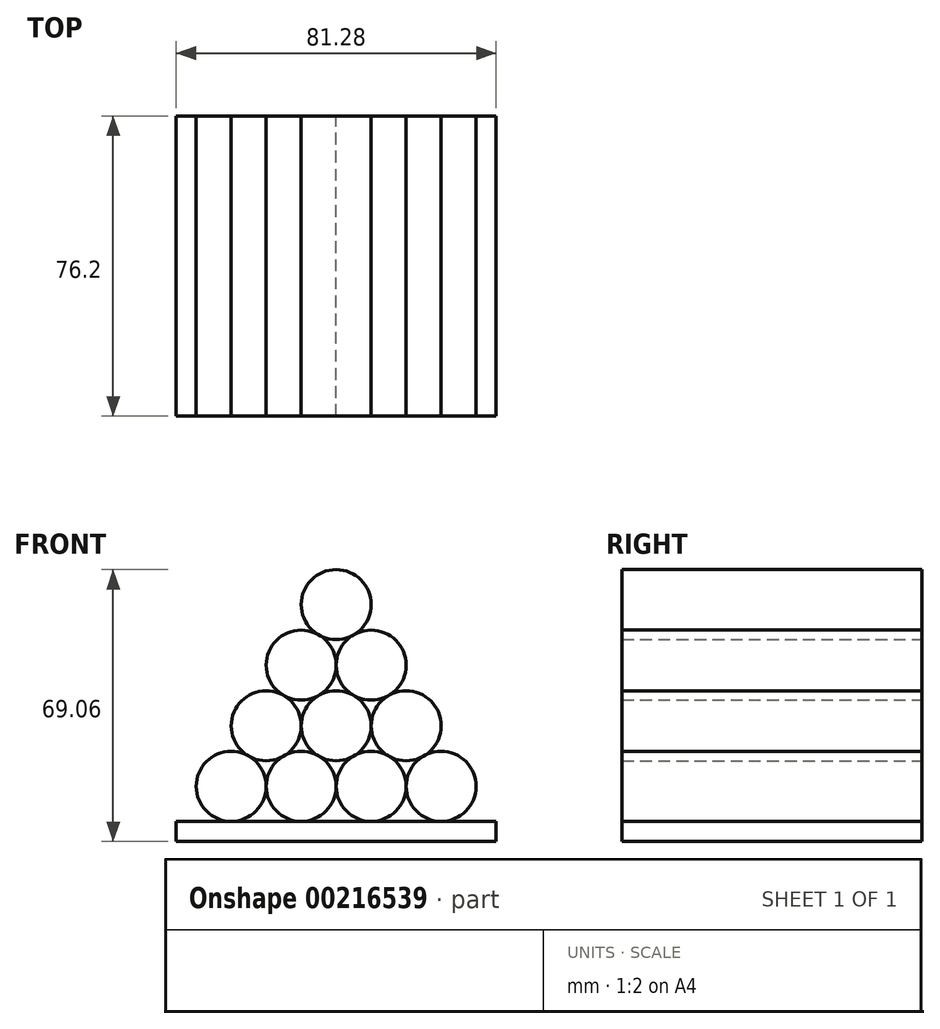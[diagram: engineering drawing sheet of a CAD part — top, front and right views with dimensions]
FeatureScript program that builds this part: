
annotation { "Feature Type Name" : "Feature", "Feature Type Description" : "" }
export const myFeature = defineFeature(function(context is Context, id is Id, definition is map)
    precondition{}
    {
        {
            var Q0;
            Q0=qCreatedBy(makeId("Front.planeOp"),FACE);
            var sketch = newSketch(context, id + "F0", { "sketchPlane" : qUnion([Q0])});
            skCircle(sketch, "E0", {"center": v(-26.67, 0) * mm, "radius": 8.9 * mm});
            skCircle(sketch, "E1", {"center": v(-8.9, 0) * mm, "radius": 8.9 * mm});
            skCircle(sketch, "E2", {"center": v(8.9, 0) * mm, "radius": 8.9 * mm});
            skCircle(sketch, "E3", {"center": v(-17.78, 15.4) * mm, "radius": 8.9 * mm});
            skCircle(sketch, "E4", {"center": v(0, 15.4) * mm, "radius": 8.9 * mm});
            skCircle(sketch, "E5", {"center": v(-8.9, 30.8) * mm, "radius": 8.9 * mm});
            skCircle(sketch, "E6", {"center": v(-35.56, -15.4) * mm, "radius": 8.9 * mm});
            skCircle(sketch, "E7", {"center": v(-17.78, -15.4) * mm, "radius": 8.9 * mm});
            skCircle(sketch, "E8", {"center": v(0, -15.4) * mm, "radius": 8.9 * mm});
            skCircle(sketch, "E9", {"center": v(17.78, -15.4) * mm, "radius": 8.9 * mm});
            skLineSegment(sketch, "E10.bottom", {"start": v(-49.53, -24.29) * mm, "end": v(31.75, -24.29) * mm});
            skLineSegment(sketch, "E10.top", {"start": v(-49.53, -29.37) * mm, "end": v(31.75, -29.37) * mm});
            skLineSegment(sketch, "E10.left", {"start": v(-49.53, -24.29) * mm, "end": v(-49.53, -29.37) * mm});
            skLineSegment(sketch, "E10.right", {"start": v(31.75, -24.29) * mm, "end": v(31.75, -29.37) * mm});
            skLineSegment(sketch, "E11", {"start": v(-8.9, 30.8) * mm, "end": v(-8.9, -46.28) * mm, "construction": true});
            skSolve(sketch);
        }
        {
            var Q0;
            {var subQ0=sQuery(id+"F0.wireOp",EDGE,"E3");var subQ1=makeQuery(id+"F0.imprint","INTERSECT",VERTEX,{"derivedFrom":[sQuery(id+"F0.wireOp",EDGE,"E0"),subQ0]});Q0=makeQuery(id+"F0.imprint","IMPRINT",FACE,{"disambiguationData":[TD([[makeQuery(id+"F0.imprint","IMPRINT",EDGE,{"disambiguationData":[TD([[subQ1,1.0]])],"derivedFrom":subQ0}),1.0]])]});}
            var Q1;
            {var subQ0=sQuery(id+"F0.wireOp",EDGE,"E4");var subQ1=makeQuery(id+"F0.imprint","INTERSECT",VERTEX,{"derivedFrom":[sQuery(id+"F0.wireOp",EDGE,"E3"),subQ0]});Q1=makeQuery(id+"F0.imprint","IMPRINT",FACE,{"disambiguationData":[TD([[makeQuery(id+"F0.imprint","IMPRINT",EDGE,{"disambiguationData":[TD([[subQ1,1.0]])],"derivedFrom":subQ0}),1.0]])]});}
            var Q2;
            {var subQ0=sQuery(id+"F0.wireOp",EDGE,"E5");var subQ1=makeQuery(id+"F0.imprint","INTERSECT",VERTEX,{"derivedFrom":[sQuery(id+"F0.wireOp",EDGE,"E4"),subQ0]});Q2=makeQuery(id+"F0.imprint","IMPRINT",FACE,{"disambiguationData":[TD([[makeQuery(id+"F0.imprint","IMPRINT",EDGE,{"disambiguationData":[TD([[subQ1,-1.0]])],"derivedFrom":subQ0}),1.0]])]});}
            var Q3;
            {var subQ0=sQuery(id+"F0.wireOp",EDGE,"6513f72b-f417-4675-a262-e46438cbcac2");var subQ1=makeQuery(id+"F0.imprint","INTERSECT",VERTEX,{"derivedFrom":[subQ0,sQuery(id+"F0.wireOp",EDGE,"E5")]});Q3=makeQuery(id+"F0.imprint","IMPRINT",FACE,{"disambiguationData":[TD([[makeQuery(id+"F0.imprint","IMPRINT",EDGE,{"disambiguationData":[TD([[subQ1,-1.0]])],"derivedFrom":subQ0}),1.0]])]});}
            var Q4;
            {var subQ0=sQuery(id+"F0.wireOp",EDGE,"E2");var subQ4=makeQuery(id+"F0.imprint","INTERSECT",VERTEX,{"derivedFrom":[subQ0,sQuery(id+"F0.wireOp",EDGE,"E5")]});Q4=makeQuery(id+"F0.imprint","IMPRINT",FACE,{"disambiguationData":[TD([[makeQuery(id+"F0.imprint","IMPRINT",EDGE,{"disambiguationData":[TD([[subQ4,1.0]])],"derivedFrom":subQ0}),1.0]])]});}
            var Q5;
            {var subQ0=sQuery(id+"F0.wireOp",EDGE,"E1");var subQ4=makeQuery(id+"F0.imprint","INTERSECT",VERTEX,{"derivedFrom":[subQ0,sQuery(id+"F0.wireOp",EDGE,"E4")]});Q5=makeQuery(id+"F0.imprint","IMPRINT",FACE,{"disambiguationData":[TD([[makeQuery(id+"F0.imprint","IMPRINT",EDGE,{"disambiguationData":[TD([[subQ4,1.0]])],"derivedFrom":subQ0}),1.0]])]});}
            var Q6;
            {var subQ0=sQuery(id+"F0.wireOp",EDGE,"E0");var subQ1=makeQuery(id+"F0.imprint","INTERSECT",VERTEX,{"derivedFrom":[subQ0,sQuery(id+"F0.wireOp",EDGE,"E3")]});Q6=makeQuery(id+"F0.imprint","IMPRINT",FACE,{"disambiguationData":[TD([[makeQuery(id+"F0.imprint","IMPRINT",EDGE,{"disambiguationData":[TD([[subQ1,1.0]])],"derivedFrom":subQ0}),1.0]])]});}
            var Q7;
            {var subQ0=sQuery(id+"F0.wireOp",EDGE,"E6");var subQ1=makeQuery(id+"F0.imprint","INTERSECT",VERTEX,{"derivedFrom":[sQuery(id+"F0.wireOp",EDGE,"E0"),subQ0]});Q7=makeQuery(id+"F0.imprint","IMPRINT",FACE,{"disambiguationData":[TD([[makeQuery(id+"F0.imprint","IMPRINT",EDGE,{"disambiguationData":[TD([[subQ1,1.0]])],"derivedFrom":subQ0}),1.0]])]});}
            var Q8;
            {var subQ0=sQuery(id+"F0.wireOp",EDGE,"E7");var subQ4=makeQuery(id+"F0.imprint","INTERSECT",VERTEX,{"derivedFrom":[sQuery(id+"F0.wireOp",EDGE,"E1"),subQ0]});Q8=makeQuery(id+"F0.imprint","IMPRINT",FACE,{"disambiguationData":[TD([[makeQuery(id+"F0.imprint","IMPRINT",EDGE,{"disambiguationData":[TD([[subQ4,1.0]])],"derivedFrom":subQ0}),1.0]])]});}
            var Q9;
            {var subQ0=sQuery(id+"F0.wireOp",EDGE,"E8");var subQ4=makeQuery(id+"F0.imprint","INTERSECT",VERTEX,{"derivedFrom":[sQuery(id+"F0.wireOp",EDGE,"E2"),subQ0]});Q9=makeQuery(id+"F0.imprint","IMPRINT",FACE,{"disambiguationData":[TD([[makeQuery(id+"F0.imprint","IMPRINT",EDGE,{"disambiguationData":[TD([[subQ4,1.0]])],"derivedFrom":subQ0}),1.0]])]});}
            var Q10;
            {var subQ0=sQuery(id+"F0.wireOp",EDGE,"E9");var subQ4=makeQuery(id+"F0.imprint","INTERSECT",VERTEX,{"derivedFrom":[sQuery(id+"F0.wireOp",EDGE,"6513f72b-f417-4675-a262-e46438cbcac2"),subQ0]});Q10=makeQuery(id+"F0.imprint","IMPRINT",FACE,{"disambiguationData":[TD([[makeQuery(id+"F0.imprint","IMPRINT",EDGE,{"disambiguationData":[TD([[subQ4,1.0]])],"derivedFrom":subQ0}),1.0]])]});}
            var Q11;
            {var subQ0=sQuery(id+"F0.wireOp",EDGE,"c8ee9c56-d4f2-4476-a657-07a7fd572b9a");var subQ1=makeQuery(id+"F0.imprint","INTERSECT",VERTEX,{"derivedFrom":[sQuery(id+"F0.wireOp",EDGE,"6513f72b-f417-4675-a262-e46438cbcac2"),subQ0]});Q11=makeQuery(id+"F0.imprint","IMPRINT",FACE,{"disambiguationData":[TD([[makeQuery(id+"F0.imprint","IMPRINT",EDGE,{"disambiguationData":[TD([[subQ1,-1.0]])],"derivedFrom":subQ0}),1.0]])]});}
            var Q12;
            Q12=makeQuery(id+"F0.imprint","IMPRINT",FACE,{"disambiguationData":[TD([[makeQuery(id+"F0.imprint","IMPRINT",EDGE,{"derivedFrom":sQuery(id+"F0.wireOp",EDGE,"E10.top")}),1.0]])]});
            var Q13;
            Q13=sQuery(id+"F0.wireOp",EDGE,"E4");
            var Q14;
            Q14=sQuery(id+"F0.wireOp",EDGE,"E5");
            var Q15;
            Q15=sQuery(id+"F0.wireOp",EDGE,"E10.bottom");
            var Q16;
            Q16=sQuery(id+"F0.wireOp",EDGE,"E1");
            var Q17;
            Q17=sQuery(id+"F0.wireOp",EDGE,"6513f72b-f417-4675-a262-e46438cbcac2");
            var Q18;
            Q18=sQuery(id+"F0.wireOp",EDGE,"E3");
            var Q19;
            Q19=sQuery(id+"F0.wireOp",EDGE,"c8ee9c56-d4f2-4476-a657-07a7fd572b9a");
            var Q20;
            Q20=sQuery(id+"F0.wireOp",EDGE,"E7");
            var Q21;
            Q21=sQuery(id+"F0.wireOp",EDGE,"E2");
            var Q22;
            Q22=sQuery(id+"F0.wireOp",EDGE,"E10.top");
            var Q23;
            Q23=sQuery(id+"F0.wireOp",EDGE,"E0");
            var Q24;
            Q24=sQuery(id+"F0.wireOp",EDGE,"E8");
            var Q25;
            Q25=sQuery(id+"F0.wireOp",EDGE,"E9");
            var Q26;
            Q26=sQuery(id+"F0.wireOp",EDGE,"E6");
            var Q27;
            Q27=sQuery(id+"F0.wireOp",EDGE,"E10.left");
            var Q28;
            Q28=sQuery(id+"F0.wireOp",EDGE,"E10.right");
            extrude(context, id + "F1", {"entities" : qUnion([Q0, Q1, Q2, Q3, Q4, Q5, Q6, Q7, Q8, Q9, Q10, Q11, Q12]), "surfaceEntities" : qUnion([Q13, Q14, Q15, Q16, Q17, Q18, Q19, Q20, Q21, Q22, Q23, Q24, Q25, Q26, Q27, Q28]), "depth" : 76.2 * mm});
        }
    });
